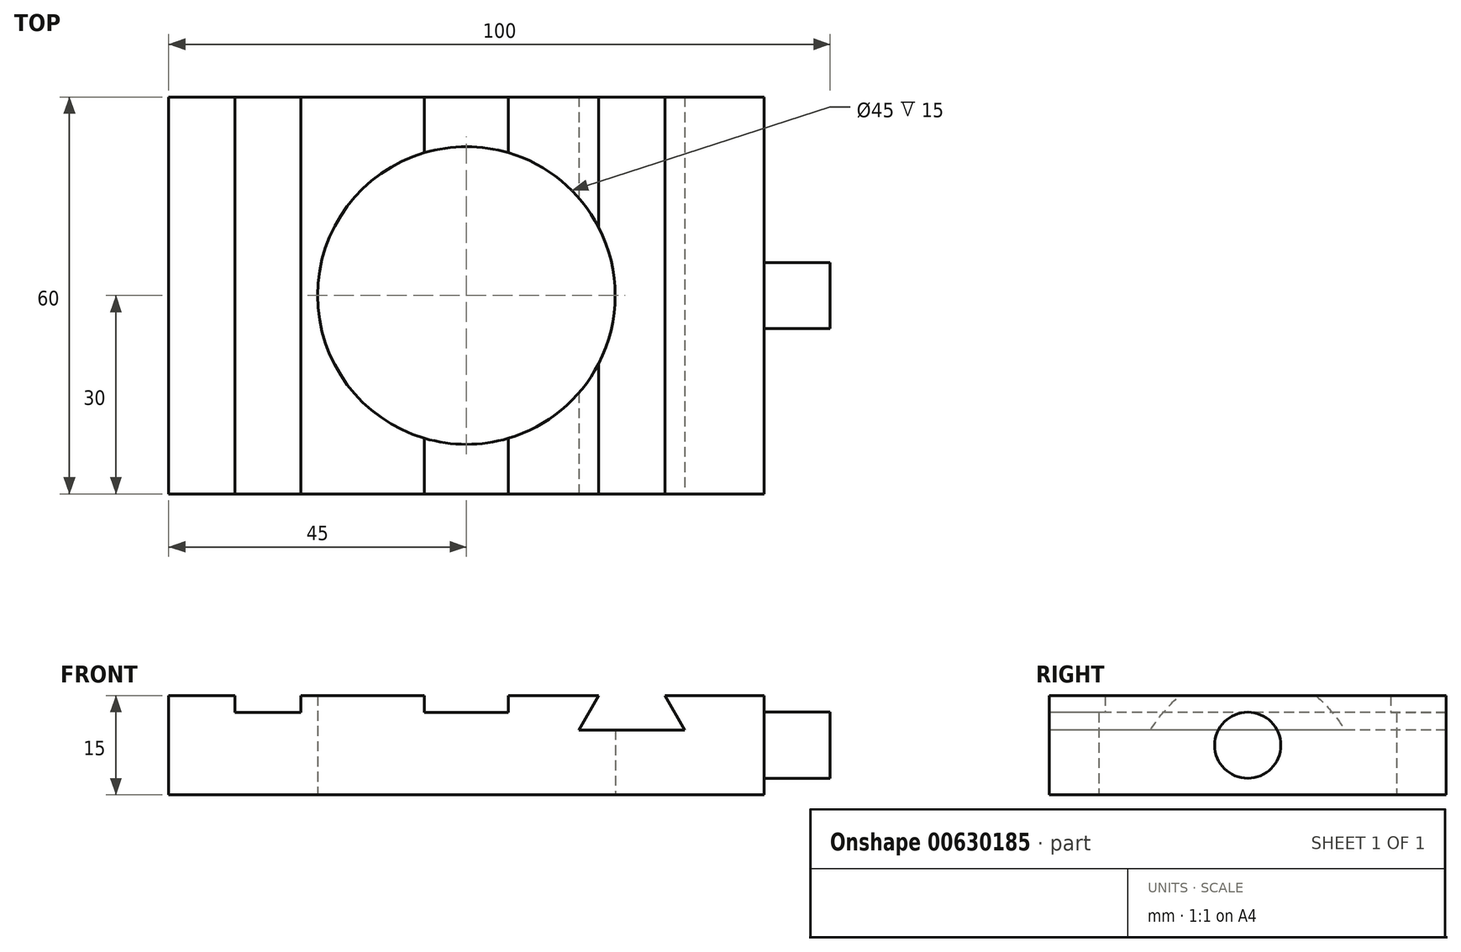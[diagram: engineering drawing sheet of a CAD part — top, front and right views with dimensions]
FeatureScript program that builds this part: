
annotation { "Feature Type Name" : "Feature", "Feature Type Description" : "" }
export const myFeature = defineFeature(function(context is Context, id is Id, definition is map)
    precondition{}
    {
        {
            var Q0;
            Q0=qCreatedBy(makeId("Top.planeOp"),FACE);
            var sketch = newSketch(context, id + "F0", { "sketchPlane" : qUnion([Q0])});
            skLineSegment(sketch, "E0.bottom", {"start": v(45, -30) * mm, "end": v(-45, -30) * mm});
            skLineSegment(sketch, "E0.top", {"start": v(45, 30) * mm, "end": v(-45, 30) * mm});
            skLineSegment(sketch, "E0.left", {"start": v(45, -30) * mm, "end": v(45, 30) * mm});
            skLineSegment(sketch, "E0.right", {"start": v(-45, -30) * mm, "end": v(-45, 30) * mm});
            skPoint(sketch, "E0.middle", {"position": v(0, 0) * mm});
            skCircle(sketch, "E1", {"center": v(0, 0) * mm, "radius": 22.5 * mm});
            skSolve(sketch);
        }
        {
            var Q0;
            Q0=makeQuery(id+"F0.imprint","IMPRINT",FACE,{"disambiguationData":[TD([[makeQuery(id+"F0.imprint","IMPRINT",EDGE,{"derivedFrom":sQuery(id+"F0.wireOp",EDGE,"E0.bottom")}),-1.0]])]});
            extrude(context, id + "F1", {"entities" : qUnion([Q0]), "depth" : 15 * mm, "offsetDistance" : 25 * mm});
        }
        {
            var Q0;
            Q0=makeQuery(id+"F1.opExtrude","CAP_FACE",FACE,{"disambiguationData":[OSD([sQuery(id+"F0.wireOp",EDGE,"E0.bottom"),sQuery(id+"F0.wireOp",EDGE,"E0.top"),sQuery(id+"F0.wireOp",EDGE,"E0.left"),sQuery(id+"F0.wireOp",EDGE,"E0.right"),sQuery(id+"F0.wireOp",EDGE,"E1")])],"isStart":false});
            var sketch = newSketch(context, id + "F2", { "sketchPlane" : qUnion([Q0])});
            skLineSegment(sketch, "E2.bottom", {"start": v(-35, 30) * mm, "end": v(-25, 30) * mm});
            skLineSegment(sketch, "E2.top", {"start": v(-35, -30) * mm, "end": v(-25, -30) * mm});
            skLineSegment(sketch, "E2.left", {"start": v(-35, 30) * mm, "end": v(-35, -30) * mm});
            skLineSegment(sketch, "E2.right", {"start": v(-25, 30) * mm, "end": v(-25, -30) * mm});
            skLineSegment(sketch, "E3", {"start": v(-6.35, 30) * mm, "end": v(-6.35, -30) * mm});
            skLineSegment(sketch, "E4", {"start": v(-6.35, -30) * mm, "end": v(6.35, -30) * mm});
            skLineSegment(sketch, "E5", {"start": v(6.35, -30) * mm, "end": v(6.35, 30) * mm});
            skLineSegment(sketch, "E6", {"start": v(6.35, 30) * mm, "end": v(-6.35, 30) * mm});
            skLineSegment(sketch, "E7", {"start": v(0, 30) * mm, "end": v(0, -30) * mm, "construction": true});
            skSolve(sketch);
        }
        {
            var Q0;
            Q0=makeQuery(id+"F2.imprint","IMPRINT",FACE,{"disambiguationData":[TD([[makeQuery(id+"F2.imprint","IMPRINT",EDGE,{"derivedFrom":sQuery(id+"F2.wireOp",EDGE,"E2.bottom")}),1.0]])]});
            var Q1;
            {var subQ0=sQuery(id+"F2.wireOp",EDGE,"E3");var subQ1=makeQuery(id+"F1.opExtrude","CAP_EDGE",EDGE,{"disambiguationData":[OSD([sQuery(id+"F0.wireOp",EDGE,"E1")])],"isStart":false});var subQ2=makeQuery(id+"F2.imprint","INTERSECT",VERTEX,{"disambiguationData":[OD(0.0)],"derivedFrom":[subQ1,subQ0]});Q1=makeQuery(id+"F2.imprint","IMPRINT",FACE,{"disambiguationData":[TD([[makeQuery(id+"F2.imprint","IMPRINT",EDGE,{"disambiguationData":[TD([[subQ2,-1.0]])],"derivedFrom":subQ0}),1.0]])]});}
            var Q2;
            {var subQ0=sQuery(id+"F2.wireOp",EDGE,"E4");Q2=makeQuery(id+"F2.imprint","IMPRINT",FACE,{"disambiguationData":[TD([[makeQuery(id+"F2.imprint","IMPRINT",EDGE,{"derivedFrom":subQ0}),-1.0]])]});}
            var Q3;
            {var subQ0=sQuery(id+"F2.wireOp",EDGE,"E6");Q3=makeQuery(id+"F2.imprint","IMPRINT",FACE,{"disambiguationData":[TD([[makeQuery(id+"F2.imprint","IMPRINT",EDGE,{"derivedFrom":subQ0}),1.0]])]});}
            extrude(context, id + "F3", {"entities" : qUnion([Q0, Q1, Q2, Q3]), "operationType" : NewBodyOperationType.REMOVE, "oppositeDirection" : true, "depth" : 2.54 * mm, "offsetDistance" : 25 * mm});
        }
        {
            var Q0;
            Q0=makeQuery(id+"F1.opExtrude","SWEPT_FACE",FACE,{"disambiguationData":[OSD([sQuery(id+"F0.wireOp",EDGE,"E0.bottom")])]});
            var sketch = newSketch(context, id + "F4", { "sketchPlane" : qUnion([Q0])});
            skLineSegment(sketch, "E8", {"start": v(20, 15) * mm, "end": v(17, 9.8) * mm});
            skLineSegment(sketch, "E9", {"start": v(17, 9.8) * mm, "end": v(33, 9.8) * mm});
            skLineSegment(sketch, "E10", {"start": v(33, 9.8) * mm, "end": v(30, 15) * mm});
            skLineSegment(sketch, "E11", {"start": v(30, 15) * mm, "end": v(20, 15) * mm});
            skLineSegment(sketch, "E12", {"start": v(25, 9.8) * mm, "end": v(25, 15) * mm, "construction": true});
            skSolve(sketch);
        }
        {
            var Q0;
            Q0=makeQuery(id+"F4.imprint","IMPRINT",FACE,{"disambiguationData":[TD([[makeQuery(id+"F4.imprint","IMPRINT",EDGE,{"derivedFrom":sQuery(id+"F4.wireOp",EDGE,"E8")}),1.0]])]});
            extrude(context, id + "F5", {"entities" : qUnion([Q0]), "operationType" : NewBodyOperationType.REMOVE, "endBound" : BoundingType.THROUGH_ALL, "oppositeDirection" : true, "depth" : 25 * mm, "offsetDistance" : 25 * mm});
        }
        {
            var Q0;
            Q0=makeQuery(id+"F1.opExtrude","SWEPT_FACE",FACE,{"disambiguationData":[OSD([sQuery(id+"F0.wireOp",EDGE,"E0.left")])]});
            var sketch = newSketch(context, id + "F6", { "sketchPlane" : qUnion([Q0])});
            skCircle(sketch, "E13", {"center": v(0, 7.5) * mm, "radius": 5 * mm});
            skPoint(sketch, "E13.centerSnap0", {"position": v(-30, 7.5) * mm});
            skPoint(sketch, "E13.centerSnap1", {"position": v(0, 15) * mm});
            skSolve(sketch);
        }
        {
            var Q0;
            Q0=makeQuery(id+"F6.imprint","IMPRINT",FACE,{"disambiguationData":[TD([[makeQuery(id+"F6.imprint","IMPRINT",EDGE,{"derivedFrom":sQuery(id+"F6.wireOp",EDGE,"E13")}),1.0]])]});
            extrude(context, id + "F7", {"entities" : qUnion([Q0]), "operationType" : NewBodyOperationType.ADD, "depth" : 10 * mm, "offsetDistance" : 25 * mm});
        }
    });
